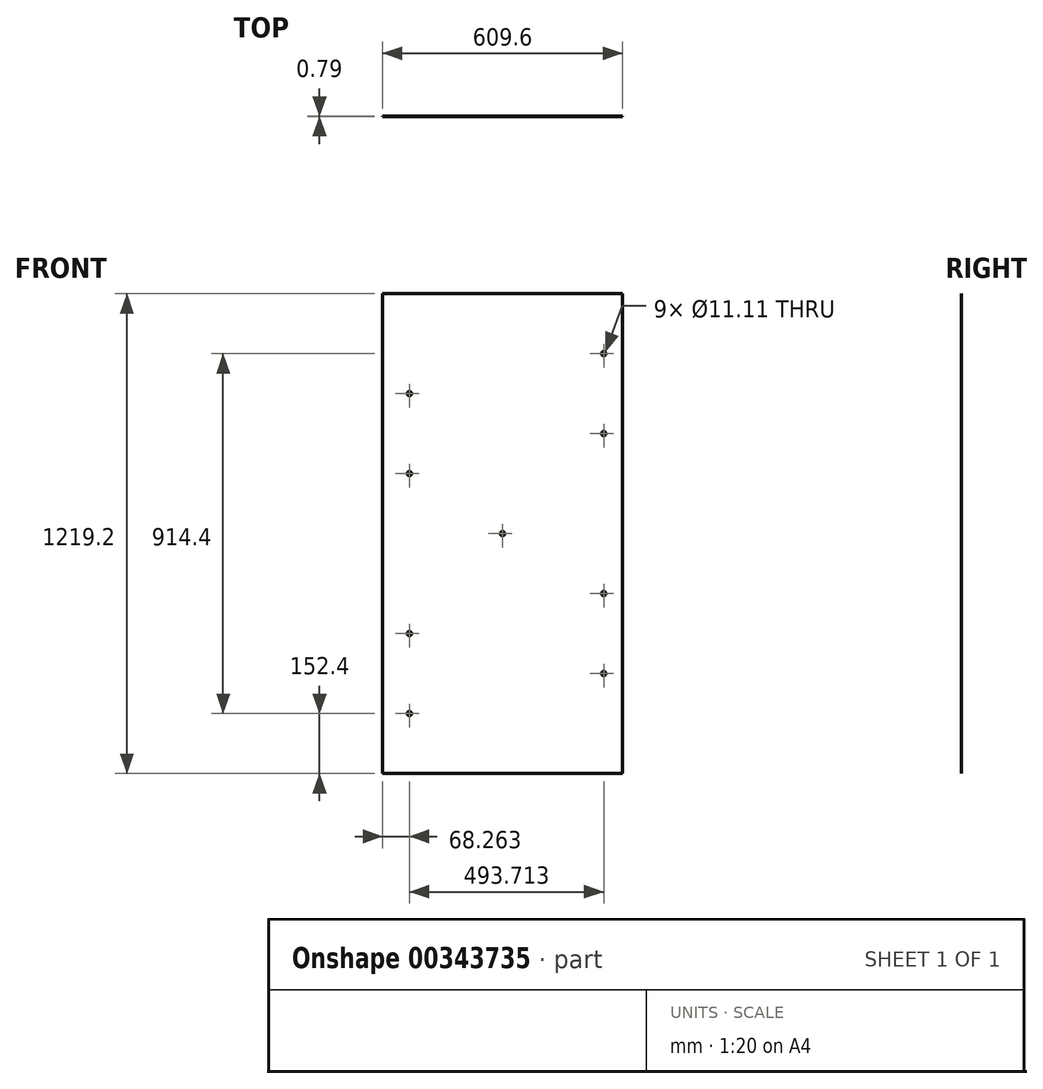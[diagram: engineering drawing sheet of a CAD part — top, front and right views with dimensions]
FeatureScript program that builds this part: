
annotation { "Feature Type Name" : "Feature", "Feature Type Description" : "" }
export const myFeature = defineFeature(function(context is Context, id is Id, definition is map)
    precondition{}
    {
        {
            var Q0;
            Q0=qCreatedBy(makeId("Front.planeOp"),FACE);
            var sketch = newSketch(context, id + "F0", { "sketchPlane" : qUnion([Q0])});
            skLineSegment(sketch, "E0.bottom", {"start": v(0, 0) * mm, "end": v(609.6, 0) * mm});
            skLineSegment(sketch, "E0.top", {"start": v(0, 1219.2) * mm, "end": v(609.6, 1219.2) * mm});
            skLineSegment(sketch, "E0.left", {"start": v(0, 0) * mm, "end": v(0, 1219.2) * mm});
            skLineSegment(sketch, "E0.right", {"start": v(609.6, 0) * mm, "end": v(609.6, 1219.2) * mm});
            skSolve(sketch);
        }
        {
            var Q0;
            Q0=makeQuery(id+"F0.imprint","IMPRINT",FACE,{"disambiguationData":[TD([[makeQuery(id+"F0.imprint","IMPRINT",EDGE,{"derivedFrom":sQuery(id+"F0.wireOp",EDGE,"E0.bottom")}),1.0]])]});
            extrude(context, id + "F1", {"entities" : qUnion([Q0]), "depth" : 0.8 * mm});
        }
        {
            var Q0;
            Q0=makeQuery(id+"F1.opExtrude","CAP_FACE",FACE,{"disambiguationData":[OSD([sQuery(id+"F0.wireOp",EDGE,"E0.bottom"),sQuery(id+"F0.wireOp",EDGE,"E0.top"),sQuery(id+"F0.wireOp",EDGE,"E0.left"),sQuery(id+"F0.wireOp",EDGE,"E0.right")])],"isStart":false});
            var sketch = newSketch(context, id + "F2", { "sketchPlane" : qUnion([Q0])});
            skCircle(sketch, "E1", {"center": v(68.26, 152.4) * mm, "radius": 5.56 * mm});
            skCircle(sketch, "E2", {"center": v(68.26, 355.6) * mm, "radius": 5.56 * mm});
            skCircle(sketch, "E3", {"center": v(561.97, 1066.8) * mm, "radius": 5.56 * mm});
            skCircle(sketch, "E4", {"center": v(561.97, 863.6) * mm, "radius": 5.56 * mm});
            skLineSegment(sketch, "E5", {"start": v(0, 609.6) * mm, "end": v(609.6, 609.6) * mm, "construction": true});
            skCircle(sketch, "E6", {"center": v(68.26, 762) * mm, "radius": 5.56 * mm});
            skCircle(sketch, "E7", {"center": v(68.26, 965.2) * mm, "radius": 5.56 * mm});
            skCircle(sketch, "E8", {"center": v(561.97, 457.2) * mm, "radius": 5.56 * mm});
            skCircle(sketch, "E9", {"center": v(561.97, 254) * mm, "radius": 5.56 * mm});
            skSolve(sketch);
        }
        {
            var Q0;
            Q0=makeQuery(id+"F2.imprint","IMPRINT",FACE,{"disambiguationData":[TD([[makeQuery(id+"F2.imprint","IMPRINT",EDGE,{"derivedFrom":sQuery(id+"F2.wireOp",EDGE,"E1")}),1.0]])]});
            var Q1;
            Q1=makeQuery(id+"F2.imprint","IMPRINT",FACE,{"disambiguationData":[TD([[makeQuery(id+"F2.imprint","IMPRINT",EDGE,{"derivedFrom":sQuery(id+"F2.wireOp",EDGE,"E2")}),1.0]])]});
            var Q2;
            Q2=makeQuery(id+"F2.imprint","IMPRINT",FACE,{"disambiguationData":[TD([[makeQuery(id+"F2.imprint","IMPRINT",EDGE,{"derivedFrom":sQuery(id+"F2.wireOp",EDGE,"E4")}),1.0]])]});
            var Q3;
            Q3=makeQuery(id+"F2.imprint","IMPRINT",FACE,{"disambiguationData":[TD([[makeQuery(id+"F2.imprint","IMPRINT",EDGE,{"derivedFrom":sQuery(id+"F2.wireOp",EDGE,"E3")}),1.0]])]});
            var Q4;
            Q4=makeQuery(id+"F2.imprint","IMPRINT",FACE,{"disambiguationData":[TD([[makeQuery(id+"F2.imprint","IMPRINT",EDGE,{"derivedFrom":sQuery(id+"F2.wireOp",EDGE,"E9")}),1.0]])]});
            var Q5;
            Q5=makeQuery(id+"F2.imprint","IMPRINT",FACE,{"disambiguationData":[TD([[makeQuery(id+"F2.imprint","IMPRINT",EDGE,{"derivedFrom":sQuery(id+"F2.wireOp",EDGE,"E8")}),1.0]])]});
            var Q6;
            Q6=makeQuery(id+"F2.imprint","IMPRINT",FACE,{"disambiguationData":[TD([[makeQuery(id+"F2.imprint","IMPRINT",EDGE,{"derivedFrom":sQuery(id+"F2.wireOp",EDGE,"E6")}),1.0]])]});
            var Q7;
            Q7=makeQuery(id+"F2.imprint","IMPRINT",FACE,{"disambiguationData":[TD([[makeQuery(id+"F2.imprint","IMPRINT",EDGE,{"derivedFrom":sQuery(id+"F2.wireOp",EDGE,"E7")}),1.0]])]});
            extrude(context, id + "F3", {"entities" : qUnion([Q0, Q1, Q2, Q3, Q4, Q5, Q6, Q7]), "operationType" : NewBodyOperationType.REMOVE, "oppositeDirection" : true, "depth" : 25.4 * mm});
        }
        {
            var Q0;
            Q0=makeQuery(id+"F1.opExtrude","CAP_FACE",FACE,{"disambiguationData":[OSD([sQuery(id+"F0.wireOp",EDGE,"E0.bottom"),sQuery(id+"F0.wireOp",EDGE,"E0.top"),sQuery(id+"F0.wireOp",EDGE,"E0.left"),sQuery(id+"F0.wireOp",EDGE,"E0.right")])],"isStart":false});
            var sketch = newSketch(context, id + "F4", { "sketchPlane" : qUnion([Q0])});
            skCircle(sketch, "E10", {"center": v(304.8, 609.6) * mm, "radius": 5.56 * mm});
            skSolve(sketch);
        }
        {
            var Q0;
            Q0=makeQuery(id+"F4.imprint","IMPRINT",FACE,{"disambiguationData":[TD([[makeQuery(id+"F4.imprint","IMPRINT",EDGE,{"derivedFrom":sQuery(id+"F4.wireOp",EDGE,"E10")}),1.0]])]});
            var Q1;
            Q1=makeQuery(id+"F4.imprint","IMPRINT",FACE,{"disambiguationData":[TD([[makeQuery(id+"F4.imprint","IMPRINT",EDGE,{"derivedFrom":sQuery(id+"F4.wireOp",EDGE,"ypEnzNDQ-77aP-9AOc-DvG6-TB8IZX9gMnFL")}),1.0]])]});
            extrude(context, id + "F5", {"entities" : qUnion([Q0, Q1]), "operationType" : NewBodyOperationType.REMOVE, "oppositeDirection" : true, "depth" : 25.4 * mm});
        }
    });
